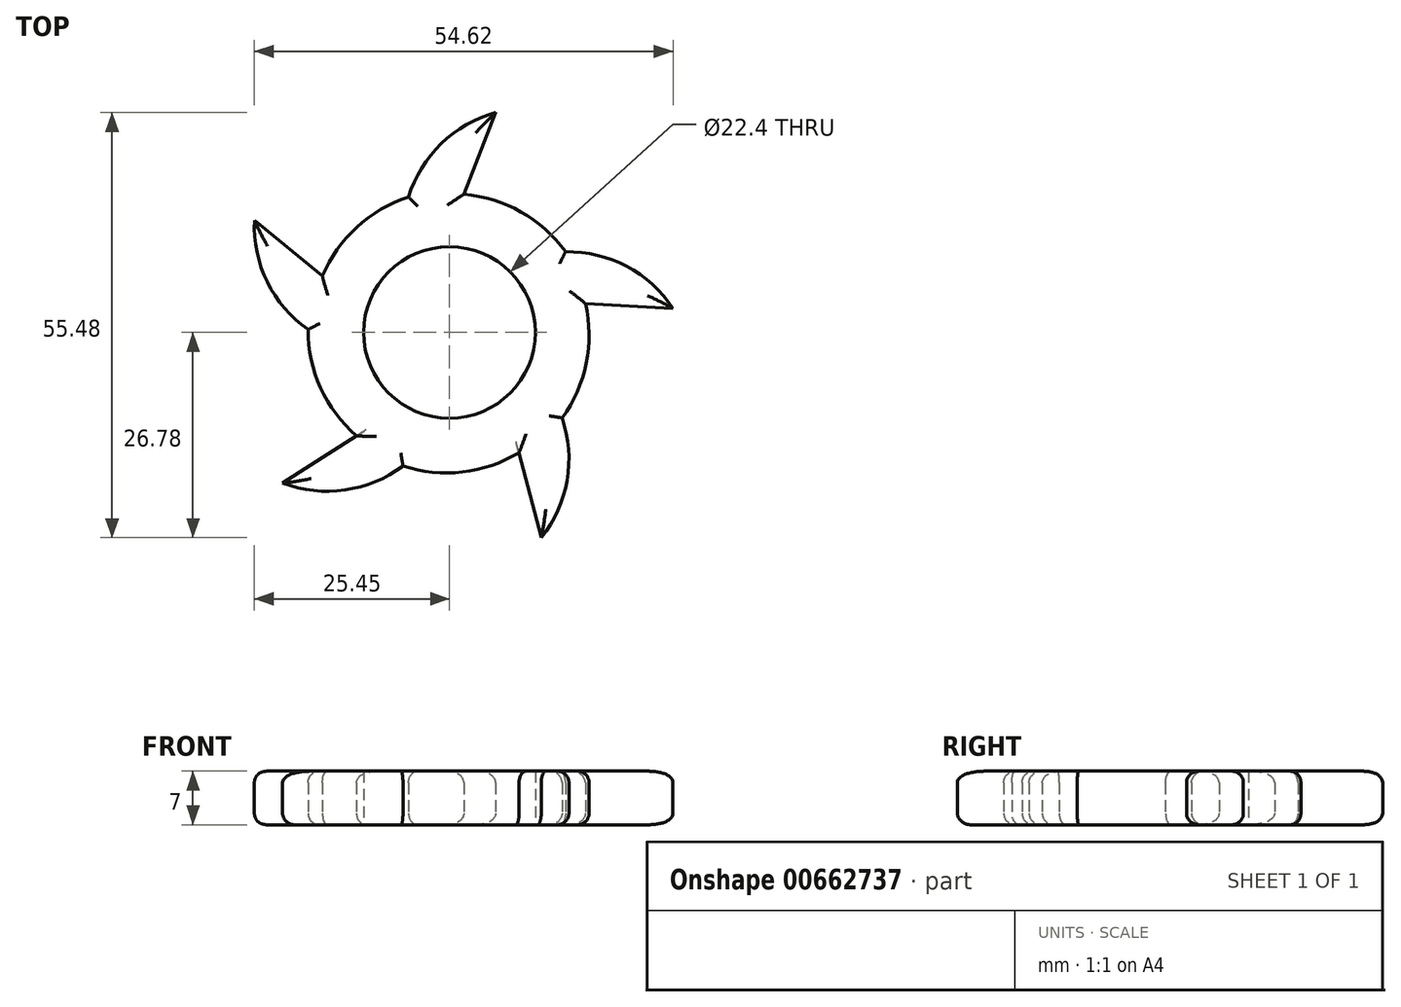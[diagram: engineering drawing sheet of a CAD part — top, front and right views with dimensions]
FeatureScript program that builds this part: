
annotation { "Feature Type Name" : "Feature", "Feature Type Description" : "" }
export const myFeature = defineFeature(function(context is Context, id is Id, definition is map)
    precondition{}
    {
        {
            var Q0;
            Q0=qCreatedBy(makeId("Top.planeOp"),FACE);
            var sketch = newSketch(context, id + "F0", { "sketchPlane" : qUnion([Q0])});
            skCircle(sketch, "E0", {"center": v(0, 0) * mm, "radius": 11.2 * mm});
            skArc(sketch, "E1", {"start": v(6.05, 28.7) * mm, "mid": v(-1.06, 24.65) * mm, "end": v(-5.34, 17.66) * mm});
            skLineSegment(sketch, "E2", {"start": v(6.05, 28.7) * mm, "end": v(1.89, 18.04) * mm});
            skArc(sketch, "E3.1.0", {"start": v(-25.43, 14.62) * mm, "mid": v(-23.77, 6.6) * mm, "end": v(-18.45, 0.38) * mm});
            skLineSegment(sketch, "E3.1.1", {"start": v(-25.43, 14.62) * mm, "end": v(-16.57, 7.37) * mm});
            skArc(sketch, "E3.2.0", {"start": v(-21.77, -19.67) * mm, "mid": v(-13.63, -20.57) * mm, "end": v(-6.06, -17.43) * mm});
            skLineSegment(sketch, "E3.2.1", {"start": v(-21.77, -19.67) * mm, "end": v(-12.13, -13.49) * mm});
            skArc(sketch, "E3.3.0", {"start": v(11.98, -26.78) * mm, "mid": v(15.35, -19.31) * mm, "end": v(14.7, -11.15) * mm});
            skLineSegment(sketch, "E3.3.1", {"start": v(11.98, -26.78) * mm, "end": v(9.08, -15.7) * mm});
            skArc(sketch, "E3.4.0", {"start": v(29.17, 3.12) * mm, "mid": v(23.11, 8.63) * mm, "end": v(15.15, 10.54) * mm});
            skLineSegment(sketch, "E3.4.1", {"start": v(29.17, 3.12) * mm, "end": v(17.74, 3.78) * mm});
            skArc(sketch, "E4", {"start": v(-5.34, 17.66) * mm, "mid": v(-12.08, 13.74) * mm, "end": v(-16.57, 7.37) * mm});
            skArc(sketch, "E5.1.0", {"start": v(-18.45, 0.38) * mm, "mid": v(-16.8, -7.24) * mm, "end": v(-12.13, -13.49) * mm});
            skArc(sketch, "E5.2.0", {"start": v(-6.06, -17.43) * mm, "mid": v(1.7, -18.22) * mm, "end": v(9.08, -15.7) * mm});
            skArc(sketch, "E5.3.0", {"start": v(14.7, -11.15) * mm, "mid": v(17.85, -4.02) * mm, "end": v(17.74, 3.78) * mm});
            skArc(sketch, "E5.4.0", {"start": v(15.15, 10.54) * mm, "mid": v(9.34, 15.74) * mm, "end": v(1.89, 18.04) * mm});
            skPoint(sketch, "E6.orphan", {"position": v(12.55, 4.08) * mm});
            skPoint(sketch, "E7.orphan", {"position": v(11.78, -5.96) * mm});
            skPoint(sketch, "E8.orphan", {"position": v(7.76, -10.68) * mm});
            skPoint(sketch, "E9.orphan", {"position": v(-2.03, -13.04) * mm});
            skPoint(sketch, "E10.orphan", {"position": v(-7.76, -10.68) * mm});
            skPoint(sketch, "E11.orphan", {"position": v(-13.03, -2.1) * mm});
            skPoint(sketch, "E12.orphan", {"position": v(-12.55, 4.08) * mm});
            skPoint(sketch, "E13.orphan", {"position": v(0, 13.2) * mm});
            skSolve(sketch);
        }
        {
            var Q0;
            Q0=makeQuery(id+"F0.imprint","IMPRINT",FACE,{"disambiguationData":[TD([[makeQuery(id+"F0.imprint","IMPRINT",EDGE,{"derivedFrom":sQuery(id+"F0.wireOp",EDGE,"E0")}),-1.0]])]});
            extrude(context, id + "F1", {"entities" : qUnion([Q0]), "depth" : 7 * mm, "offsetDistance" : 25 * mm});
        }
        {
            var Q0;
            Q0=makeQuery(id+"F1.opExtrude","CAP_EDGE",EDGE,{"disambiguationData":[OSD([sQuery(id+"F0.wireOp",EDGE,"E3.2.0")])],"isStart":false});
            var Q1;
            Q1=makeQuery(id+"F1.opExtrude","CAP_EDGE",EDGE,{"disambiguationData":[OSD([sQuery(id+"F0.wireOp",EDGE,"E5.2.0")])],"isStart":false});
            var Q2;
            Q2=makeQuery(id+"F1.opExtrude","CAP_EDGE",EDGE,{"disambiguationData":[OSD([sQuery(id+"F0.wireOp",EDGE,"E3.3.0")])],"isStart":false});
            var Q3;
            Q3=makeQuery(id+"F1.opExtrude","CAP_EDGE",EDGE,{"disambiguationData":[OSD([sQuery(id+"F0.wireOp",EDGE,"E3.3.1")])],"isStart":false});
            var Q4;
            Q4=makeQuery(id+"F1.opExtrude","CAP_EDGE",EDGE,{"disambiguationData":[OSD([sQuery(id+"F0.wireOp",EDGE,"E5.3.0")])],"isStart":false});
            var Q5;
            Q5=makeQuery(id+"F1.opExtrude","CAP_EDGE",EDGE,{"disambiguationData":[OSD([sQuery(id+"F0.wireOp",EDGE,"E3.4.0")])],"isStart":false});
            var Q6;
            Q6=makeQuery(id+"F1.opExtrude","CAP_EDGE",EDGE,{"disambiguationData":[OSD([sQuery(id+"F0.wireOp",EDGE,"E3.4.1")])],"isStart":false});
            var Q7;
            Q7=makeQuery(id+"F1.opExtrude","CAP_EDGE",EDGE,{"disambiguationData":[OSD([sQuery(id+"F0.wireOp",EDGE,"E5.4.0")])],"isStart":false});
            var Q8;
            Q8=makeQuery(id+"F1.opExtrude","CAP_EDGE",EDGE,{"disambiguationData":[OSD([sQuery(id+"F0.wireOp",EDGE,"E1")])],"isStart":false});
            var Q9;
            Q9=makeQuery(id+"F1.opExtrude","CAP_EDGE",EDGE,{"disambiguationData":[OSD([sQuery(id+"F0.wireOp",EDGE,"E2")])],"isStart":false});
            var Q10;
            Q10=makeQuery(id+"F1.opExtrude","CAP_EDGE",EDGE,{"disambiguationData":[OSD([sQuery(id+"F0.wireOp",EDGE,"E4")])],"isStart":false});
            var Q11;
            Q11=makeQuery(id+"F1.opExtrude","CAP_EDGE",EDGE,{"disambiguationData":[OSD([sQuery(id+"F0.wireOp",EDGE,"E3.1.1")])],"isStart":false});
            var Q12;
            Q12=makeQuery(id+"F1.opExtrude","CAP_EDGE",EDGE,{"disambiguationData":[OSD([sQuery(id+"F0.wireOp",EDGE,"E3.1.0")])],"isStart":false});
            var Q13;
            Q13=makeQuery(id+"F1.opExtrude","CAP_EDGE",EDGE,{"disambiguationData":[OSD([sQuery(id+"F0.wireOp",EDGE,"E5.1.0")])],"isStart":false});
            var Q14;
            Q14=makeQuery(id+"F1.opExtrude","CAP_EDGE",EDGE,{"disambiguationData":[OSD([sQuery(id+"F0.wireOp",EDGE,"E3.2.1")])],"isStart":false});
            var Q15;
            Q15=makeQuery(id+"F1.opExtrude","CAP_EDGE",EDGE,{"disambiguationData":[OSD([sQuery(id+"F0.wireOp",EDGE,"E3.3.0")])],"isStart":true});
            var Q16;
            Q16=makeQuery(id+"F1.opExtrude","CAP_EDGE",EDGE,{"disambiguationData":[OSD([sQuery(id+"F0.wireOp",EDGE,"E5.3.0")])],"isStart":true});
            var Q17;
            Q17=makeQuery(id+"F1.opExtrude","CAP_EDGE",EDGE,{"disambiguationData":[OSD([sQuery(id+"F0.wireOp",EDGE,"E3.4.1")])],"isStart":true});
            var Q18;
            Q18=makeQuery(id+"F1.opExtrude","CAP_EDGE",EDGE,{"disambiguationData":[OSD([sQuery(id+"F0.wireOp",EDGE,"E5.2.0")])],"isStart":true});
            var Q19;
            Q19=makeQuery(id+"F1.opExtrude","CAP_EDGE",EDGE,{"disambiguationData":[OSD([sQuery(id+"F0.wireOp",EDGE,"E3.2.0")])],"isStart":true});
            var Q20;
            Q20=makeQuery(id+"F1.opExtrude","CAP_EDGE",EDGE,{"disambiguationData":[OSD([sQuery(id+"F0.wireOp",EDGE,"E5.1.0")])],"isStart":true});
            var Q21;
            Q21=makeQuery(id+"F1.opExtrude","CAP_EDGE",EDGE,{"disambiguationData":[OSD([sQuery(id+"F0.wireOp",EDGE,"E3.1.0")])],"isStart":true});
            var Q22;
            Q22=makeQuery(id+"F1.opExtrude","CAP_EDGE",EDGE,{"disambiguationData":[OSD([sQuery(id+"F0.wireOp",EDGE,"E4")])],"isStart":true});
            var Q23;
            Q23=makeQuery(id+"F1.opExtrude","CAP_EDGE",EDGE,{"disambiguationData":[OSD([sQuery(id+"F0.wireOp",EDGE,"E3.1.1")])],"isStart":true});
            var Q24;
            Q24=makeQuery(id+"F1.opExtrude","CAP_EDGE",EDGE,{"disambiguationData":[OSD([sQuery(id+"F0.wireOp",EDGE,"E1")])],"isStart":true});
            var Q25;
            Q25=makeQuery(id+"F1.opExtrude","CAP_EDGE",EDGE,{"disambiguationData":[OSD([sQuery(id+"F0.wireOp",EDGE,"E2")])],"isStart":true});
            var Q26;
            Q26=makeQuery(id+"F1.opExtrude","CAP_EDGE",EDGE,{"disambiguationData":[OSD([sQuery(id+"F0.wireOp",EDGE,"E3.4.0")])],"isStart":true});
            var Q27;
            Q27=makeQuery(id+"F1.opExtrude","CAP_EDGE",EDGE,{"disambiguationData":[OSD([sQuery(id+"F0.wireOp",EDGE,"E5.4.0")])],"isStart":true});
            fillet(context, id + "F2", {"entities" : qUnion([Q0, Q1, Q2, Q3, Q4, Q5, Q6, Q7, Q8, Q9, Q10, Q11, Q12, Q13, Q14, Q15, Q16, Q17, Q18, Q19, Q20, Q21, Q22, Q23, Q24, Q25, Q26, Q27]), "radius" : 1.5 * mm, "tangentPropagation" : true, "allowEdgeOverflow" : false});
        }
    });
